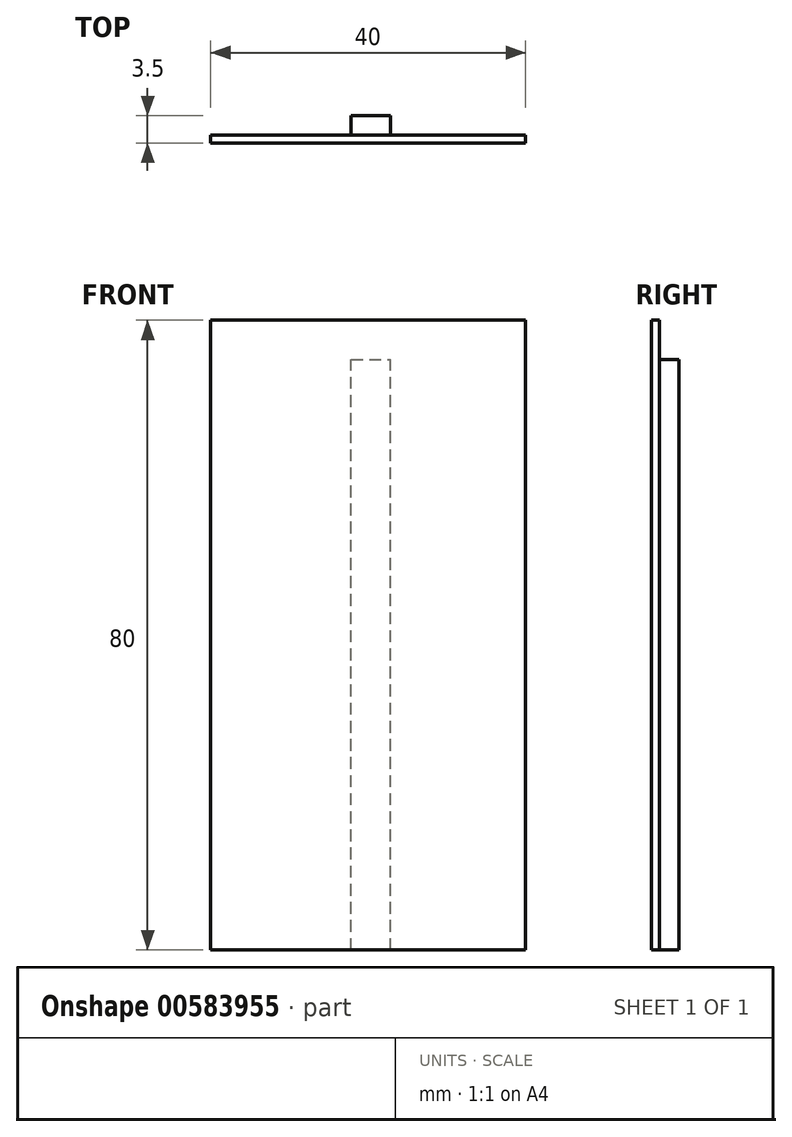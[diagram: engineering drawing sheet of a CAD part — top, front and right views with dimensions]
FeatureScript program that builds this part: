
annotation { "Feature Type Name" : "Feature", "Feature Type Description" : "" }
export const myFeature = defineFeature(function(context is Context, id is Id, definition is map)
    precondition{}
    {
        {
            var Q0;
            Q0=qCreatedBy(makeId("Front.planeOp"),FACE);
            var sketch = newSketch(context, id + "F0", { "sketchPlane" : qUnion([Q0])});
            skLineSegment(sketch, "E0.bottom", {"start": v(-20, 40) * mm, "end": v(20, 40) * mm});
            skLineSegment(sketch, "E0.top", {"start": v(-20, -40) * mm, "end": v(20, -40) * mm});
            skLineSegment(sketch, "E0.left", {"start": v(-20, 40) * mm, "end": v(-20, -40) * mm});
            skLineSegment(sketch, "E0.right", {"start": v(20, 40) * mm, "end": v(20, -40) * mm});
            skPoint(sketch, "E0.middle", {"position": v(0, 0) * mm});
            skSolve(sketch);
        }
        {
            var Q0;
            Q0=makeQuery(id+"F0.imprint","IMPRINT",FACE,{"disambiguationData":[TD([[makeQuery(id+"F0.imprint","IMPRINT",EDGE,{"derivedFrom":sQuery(id+"F0.wireOp",EDGE,"E0.bottom")}),-1.0]])]});
            extrude(context, id + "F1", {"entities" : qUnion([Q0]), "depth" : 1 * mm, "offsetDistance" : 25.4 * mm});
        }
        {
            var Q0;
            Q0=makeQuery(id+"F1.opExtrude","CAP_FACE",FACE,{"disambiguationData":[OSD([sQuery(id+"F0.wireOp",EDGE,"E0.bottom"),sQuery(id+"F0.wireOp",EDGE,"E0.top"),sQuery(id+"F0.wireOp",EDGE,"E0.left"),sQuery(id+"F0.wireOp",EDGE,"E0.right")])],"isStart":true});
            var sketch = newSketch(context, id + "F2", { "sketchPlane" : qUnion([Q0])});
            skLineSegment(sketch, "E1.bottom", {"start": v(2.14, -40) * mm, "end": v(-2.86, -40) * mm});
            skLineSegment(sketch, "E1.top", {"start": v(2.14, 35) * mm, "end": v(-2.86, 35) * mm});
            skLineSegment(sketch, "E1.left", {"start": v(2.14, -40) * mm, "end": v(2.14, 35) * mm});
            skLineSegment(sketch, "E1.right", {"start": v(-2.86, -40) * mm, "end": v(-2.86, 35) * mm});
            skSolve(sketch);
        }
        {
            var Q0;
            Q0=makeQuery(id+"F2.imprint","IMPRINT",FACE,{"disambiguationData":[TD([[makeQuery(id+"F2.imprint","IMPRINT",EDGE,{"derivedFrom":sQuery(id+"F2.wireOp",EDGE,"E1.bottom")}),-1.0]])]});
            extrude(context, id + "F3", {"entities" : qUnion([Q0]), "operationType" : NewBodyOperationType.ADD, "depth" : 2.5 * mm, "offsetDistance" : 25.4 * mm});
        }
    });
